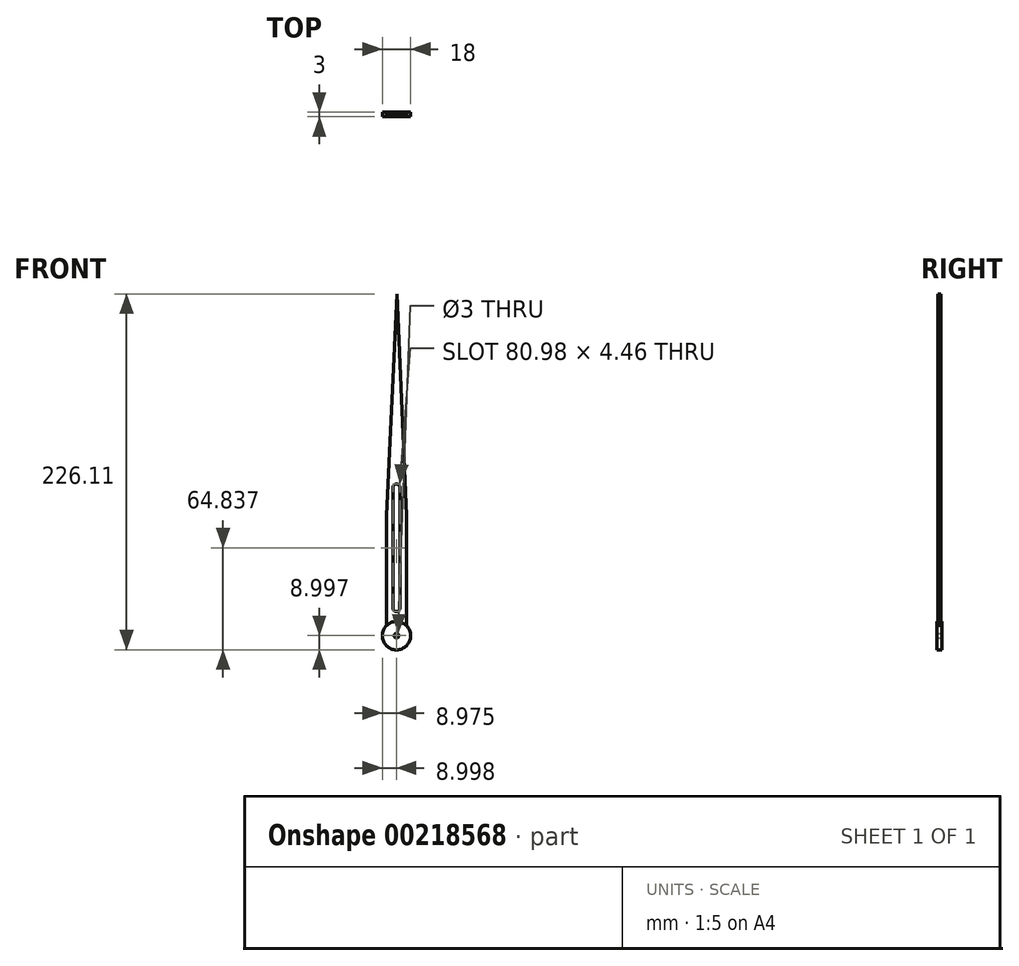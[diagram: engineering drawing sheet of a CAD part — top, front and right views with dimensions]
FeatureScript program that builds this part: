
annotation { "Feature Type Name" : "Feature", "Feature Type Description" : "" }
export const myFeature = defineFeature(function(context is Context, id is Id, definition is map)
    precondition{}
    {
        {
            var Q0;
            Q0=qCreatedBy(makeId("Front.planeOp"),FACE);
            var sketch = newSketch(context, id + "F0", { "sketchPlane" : qUnion([Q0])});
            skCircle(sketch, "E0", {"center": v(-20.04, -44.31) * mm, "radius": 1.5 * mm});
            skCircle(sketch, "E1", {"center": v(-20.04, -44.31) * mm, "radius": 9 * mm});
            skLineSegment(sketch, "E2.left", {"start": v(-26.41, -37.96) * mm, "end": v(-26.41, 32.04) * mm});
            skLineSegment(sketch, "E3.MirrorCS", {"start": v(-13.67, -37.96) * mm, "end": v(-13.67, 32.04) * mm});
            skArc(sketch, "E4", {"start": v(-22.3, -27.34) * mm, "mid": v(-20.02, -28.97) * mm, "end": v(-17.83, -27.21) * mm});
            skArc(sketch, "E5", {"start": v(-17.83, 49.79) * mm, "mid": v(-20.13, 52.02) * mm, "end": v(-22.3, 49.66) * mm});
            skLineSegment(sketch, "E6.MirrorCS", {"start": v(-22.3, 49.66) * mm, "end": v(-22.3, -27.34) * mm});
            skLineSegment(sketch, "E7", {"start": v(-17.83, 49.79) * mm, "end": v(-17.83, -27.21) * mm});
            skLineSegment(sketch, "E8", {"start": v(-19.75, 172.8) * mm, "end": v(-26.41, 32.04) * mm});
            skLineSegment(sketch, "E9.MirrorCS", {"start": v(-19.75, 172.8) * mm, "end": v(-13.67, 32.04) * mm});
            skSolve(sketch);
        }
        {
            var Q0;
            Q0=makeQuery(id+"F0.imprint","IMPRINT",FACE,{"disambiguationData":[TD([[makeQuery(id+"F0.imprint","IMPRINT",EDGE,{"derivedFrom":sQuery(id+"F0.wireOp",EDGE,"E0")}),-1.0]])]});
            var Q1;
            Q1=sQuery(id+"F0.wireOp",EDGE,"p5VHldXC-XaDy-Jo6Q-gzRM-BKwmdG1nrnMR");
            var Q2;
            Q2=sQuery(id+"F0.wireOp",EDGE,"WyDkhZpA-9s04-8oUv-ohR5-d8g4u36zodpv");
            var Q3;
            Q3=sQuery(id+"F0.wireOp",EDGE,"zPygVgP6-IXea-uzZJ-7nVa-Sz4MqIU0xlYZ");
            extrude(context, id + "F1", {"entities" : qUnion([Q0]), "surfaceEntities" : qUnion([Q1, Q2, Q3]), "depth" : 3 * mm, "symmetric" : true});
        }
        {
            var Q0;
            Q0=makeQuery(id+"F0.imprint","IMPRINT",FACE,{"disambiguationData":[TD([[makeQuery(id+"F0.imprint","IMPRINT",EDGE,{"derivedFrom":sQuery(id+"F0.wireOp",EDGE,"64VVkBTR-3lK9-xNKO-ebiv-tDq6J559YHrB.left")}),-1.0]])]});
            var Q1;
            {var subQ4=sQuery(id+"F0.wireOp",EDGE,"E2.left");Q1=makeQuery(id+"F0.imprint","IMPRINT",FACE,{"disambiguationData":[TD([[makeQuery(id+"F0.imprint","IMPRINT",EDGE,{"derivedFrom":subQ4}),-1.0]])]});}
            extrude(context, id + "F2", {"entities" : qUnion([Q0, Q1]), "operationType" : NewBodyOperationType.ADD, "depth" : 2 * mm, "symmetric" : true});
        }
    });
